# Revit family: Wall_Hung _Multiple_Station_Hand_Wash_Sink-Elkay-EWMA4820_2_4
name_source: partatom
category: Plumbing Fixtures
units: mm (PartAtom-declared; Revit-internal decimal feet)

## family parameters
Cut with Voids When Loaded = No
Host = Face
Maintain Annotation Orientation = No
OmniClass Number = 23.45.05.14.14
OmniClass Title = Sinks/Lavatories
Part Type = Normal
Room Calculation Point = No
Round Connector Dimension = Use Diameter
Shared = No

## types (2) — shared parameters
2 Holes = Yes
Approx. Shipping Weight (lbs) = 76
Assembly Code = D2010400
Back splash Height = 10.00"
Back splash width = 2.00"
Bowl  Dimensions = 45 inch x 16 1/2 inch x 8 inch
Bowl Width = 16.50"
Bowl length = 45.00"
C/C distance of holes = 32.00"
CL of Hole = 3.50"
Default Elevation = 48.00"
Distance b/w 2 Holes = 16.00"
Drain Location = Center
Drain Location along x-axis = 22.50"
Drain Location along y-axis = 6.88"
Front rim = 1.50"
Guage = 14
Installation type = Wall Hung
Main Material = Finish-Elkay-Stainless Steel
Manufacturer = Elkay Manufacturer Company
Manufacturer Brand = Elkay (by Zurn Elkay Water Solutions)
No of Bowls = 1
Outlet Connection Size (inch) = 1.50"
Product Documentation Link = https://www.elkayfiles.com
Product Installation Sheet URL = https://www.elkayfiles.com
Product Page URL = https://www.elkay.com
Product Weight (lbs) = 75
Product data URL = https://www.bimobject.com
Repair Parts URL = https://www.elkayfiles.com
Rim = 1.50"
Sink Depth = 18.00"
Sink Dimensions = 48 inch x 20 inch x 18 inch
Sink Length = 48.00"
Sink Width = 20.00"
URL = https://www.elkay.com

## per-type parameters (varying)
| type | 4 Holes | Description | Drain Size | Model |
| EWMA48202(Wall Hung Multiple Station 2-Hole Sink) | No | Stainless Steel 48 inch x 20 inch x 18 inch 2-Hole Wall Hung Multiple Station Hand Wash Sink | 3 1/2 inch | EWMA48202 |
| EWMA48204(Wall Hung Multiple Station 4-Hole Sink) | Yes | Stainless Steel 48 inch x 20 inch x 18 inch 4-Hole Wall Hung Multiple Station Hand Wash Sink | 3 1/2 | EWMA48204 |

## geometry (parser evidence)
native form markers: Sweep x6
no freeform markers — native parametric forms only
